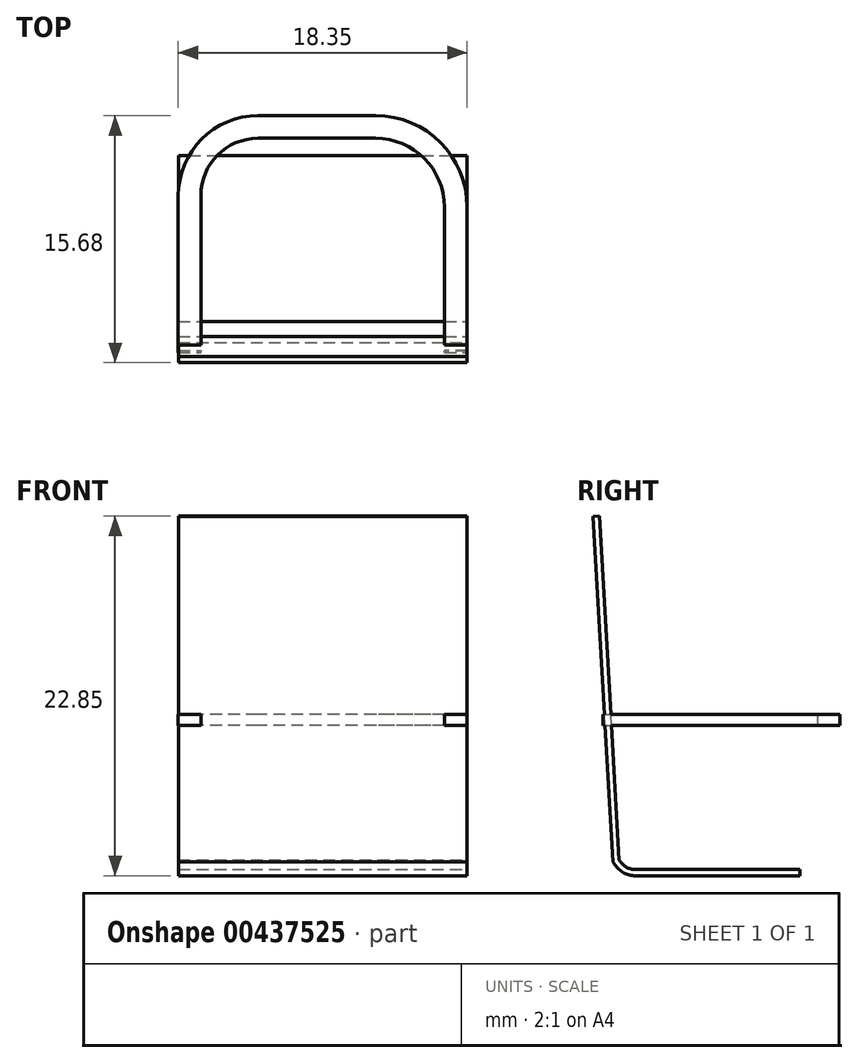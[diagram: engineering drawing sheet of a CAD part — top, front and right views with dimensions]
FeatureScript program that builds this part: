
annotation { "Feature Type Name" : "Feature", "Feature Type Description" : "" }
export const myFeature = defineFeature(function(context is Context, id is Id, definition is map)
    precondition{}
    {
        {
            var Q0;
            Q0=qCreatedBy(makeId("Top.planeOp"),FACE);
            var sketch = newSketch(context, id + "F0", { "sketchPlane" : qUnion([Q0])});
            skLineSegment(sketch, "E0.top", {"start": v(-5.8, 15.04) * mm, "end": v(-13.28, 15.04) * mm});
            skLineSegment(sketch, "E0.left", {"start": v(0, 0) * mm, "end": v(0, 9.23) * mm});
            skLineSegment(sketch, "E0.right", {"start": v(-18.35, 0) * mm, "end": v(-18.35, 9.97) * mm});
            skPoint(sketch, "E1.visualSharp", {"position": v(-18.35, 15.04) * mm});
            skArc(sketch, "E1.filletArc", {"start": v(-13.28, 15.04) * mm, "mid": v(-16.86, 13.56) * mm, "end": v(-18.35, 9.97) * mm});
            skPoint(sketch, "E2.visualSharp", {"position": v(0, 15.04) * mm});
            skArc(sketch, "E2.filletArc", {"start": v(0, 9.23) * mm, "mid": v(-1.7, 13.34) * mm, "end": v(-5.8, 15.04) * mm});
            skLineSegment(sketch, "E3.0", {"start": v(-1.44, 0) * mm, "end": v(-1.44, 9.23) * mm});
            skLineSegment(sketch, "E3.1", {"start": v(-16.91, 0) * mm, "end": v(-16.91, 9.97) * mm});
            skArc(sketch, "E3.2", {"start": v(-13.28, 13.6) * mm, "mid": v(-15.85, 12.54) * mm, "end": v(-16.91, 9.97) * mm});
            skLineSegment(sketch, "E3.3", {"start": v(-5.8, 13.6) * mm, "end": v(-13.28, 13.6) * mm});
            skArc(sketch, "E3.4", {"start": v(-1.44, 9.23) * mm, "mid": v(-2.72, 12.32) * mm, "end": v(-5.8, 13.6) * mm});
            skLineSegment(sketch, "E4", {"start": v(-18.35, 0) * mm, "end": v(-16.91, 0) * mm});
            skLineSegment(sketch, "E5", {"start": v(-1.44, 0) * mm, "end": v(0, 0) * mm});
            skSolve(sketch);
        }
        {
            var Q0;
            Q0=qCreatedBy(makeId("Right.planeOp"),FACE);
            var sketch = newSketch(context, id + "F1", { "sketchPlane" : qUnion([Q0])});
            skLineSegment(sketch, "E6", {"start": v(-0.64, 13.28) * mm, "end": v(0.63, -8.66) * mm});
            skArc(sketch, "E7", {"start": v(0.63, -8.66) * mm, "mid": v(1.18, -9.28) * mm, "end": v(1.96, -9.55) * mm});
            skLineSegment(sketch, "E8", {"start": v(1.96, -9.55) * mm, "end": v(10.39, -9.55) * mm});
            skLineSegment(sketch, "E9.0", {"start": v(1.97, -9.15) * mm, "end": v(10.39, -9.15) * mm});
            skArc(sketch, "E9.1", {"start": v(1.02, -8.55) * mm, "mid": v(1.42, -8.97) * mm, "end": v(1.97, -9.15) * mm});
            skLineSegment(sketch, "E9.2", {"start": v(-0.24, 13.3) * mm, "end": v(1.02, -8.55) * mm});
            skLineSegment(sketch, "E10", {"start": v(10.39, -9.15) * mm, "end": v(10.39, -9.55) * mm});
            skLineSegment(sketch, "E11", {"start": v(-0.64, 13.28) * mm, "end": v(-0.24, 13.3) * mm});
            skSolve(sketch);
        }
        {
            var Q0;
            Q0 = qSketchRegion(id + "F1", true);
            extrude(context, id + "F2", {"entities" : qUnion([Q0]), "oppositeDirection" : true, "depth" : 1.65 * mm});
        }
        {
            var Q0;
            Q0=makeQuery(id+"F0.imprint","IMPRINT",FACE,{"disambiguationData":[TD([[makeQuery(id+"F0.imprint","IMPRINT",EDGE,{"derivedFrom":sQuery(id+"F0.wireOp",EDGE,"E0.top")}),1.0]])]});
            extrude(context, id + "F3", {"entities" : qUnion([Q0]), "operationType" : NewBodyOperationType.ADD, "depth" : 0.71 * mm});
        }
        {
            var Q0;
            Q0=makeQuery(id+"F2.opExtrude","CAP_FACE",FACE,{"disambiguationData":[OSD([sQuery(id+"F1.wireOp",EDGE,"E6"),sQuery(id+"F1.wireOp",EDGE,"E7"),sQuery(id+"F1.wireOp",EDGE,"E8"),sQuery(id+"F1.wireOp",EDGE,"E9.0"),sQuery(id+"F1.wireOp",EDGE,"E9.1"),sQuery(id+"F1.wireOp",EDGE,"E9.2"),sQuery(id+"F1.wireOp",EDGE,"E10"),sQuery(id+"F1.wireOp",EDGE,"E11")])],"isStart":false});
            extrude(context, id + "F4", {"entities" : qUnion([Q0]), "operationType" : NewBodyOperationType.ADD, "depth" : 16.7 * mm});
        }
        {
            var Q0;
            {var subQ0=sQuery(id+"F1.wireOp",EDGE,"E10");Q0=makeQuery(id+"F4.boolean.opBoolean","MERGE",FACE,{"derivedFrom":[makeQuery(id+"F2.opExtrude","SWEPT_FACE",FACE,{"disambiguationData":[OSD([subQ0])]}),makeQuery(id+"F4.opExtrude","SWEPT_FACE",FACE,{"disambiguationData":[OSD([subQ0])]})]});}
            extrude(context, id + "F5", {"entities" : qUnion([Q0]), "operationType" : NewBodyOperationType.ADD, "depth" : 2.1 * mm});
        }
    });
